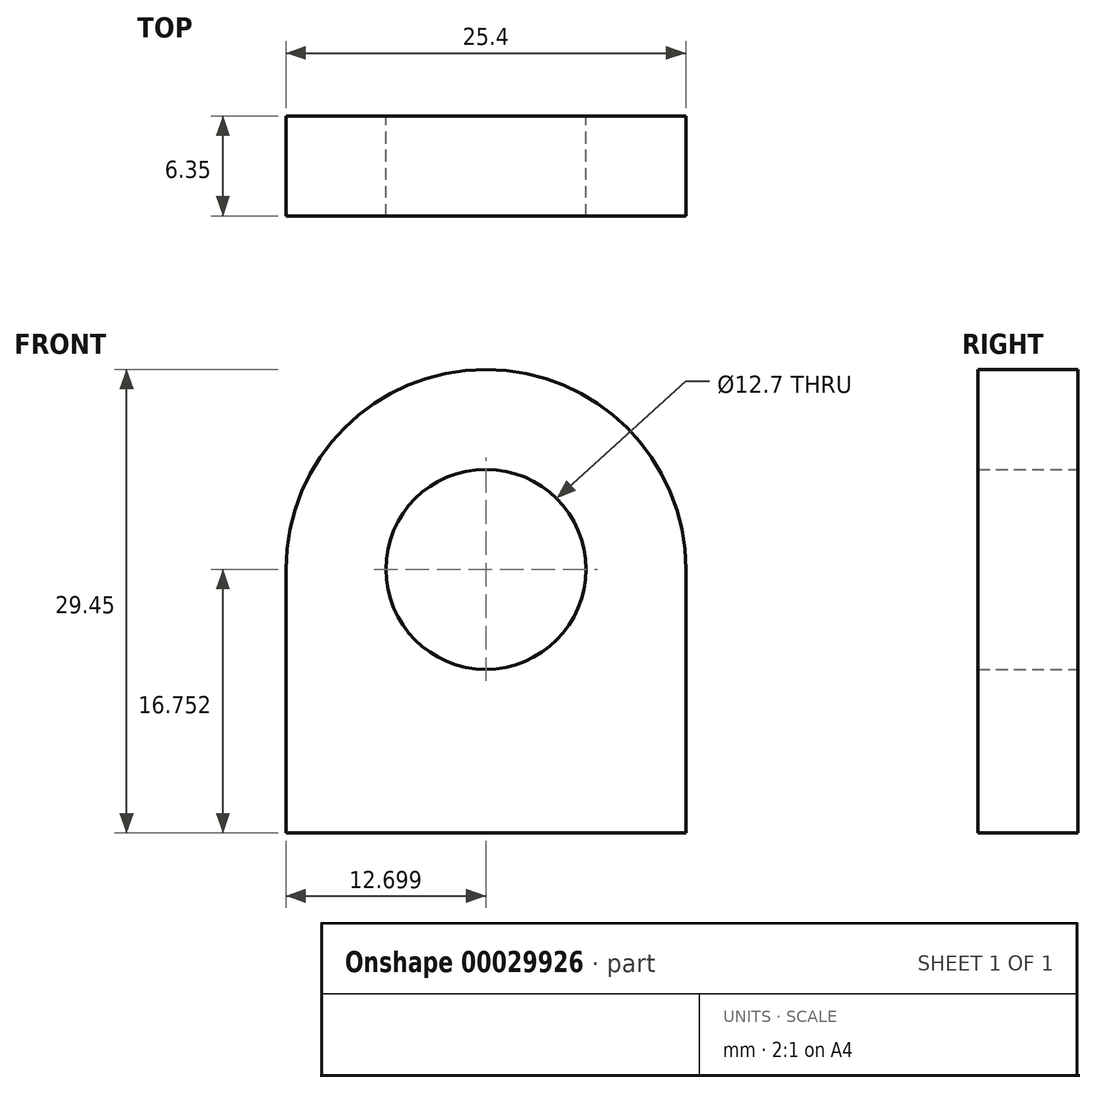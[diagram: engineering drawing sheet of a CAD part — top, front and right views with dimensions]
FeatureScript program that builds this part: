
annotation { "Feature Type Name" : "Feature", "Feature Type Description" : "" }
export const myFeature = defineFeature(function(context is Context, id is Id, definition is map)
    precondition{}
    {
        {
            var Q0;
            Q0=qCreatedBy(makeId("Front.planeOp"),FACE);
            var sketch = newSketch(context, id + "F0", { "sketchPlane" : qUnion([Q0])});
            skLineSegment(sketch, "E0.top", {"start": v(-5.45, 2.81) * mm, "end": v(19.95, 2.81) * mm});
            skLineSegment(sketch, "E0.left", {"start": v(-5.45, 19.56) * mm, "end": v(-5.45, 2.81) * mm});
            skLineSegment(sketch, "E0.right", {"start": v(19.95, 19.56) * mm, "end": v(19.95, 2.81) * mm});
            skArc(sketch, "E1", {"start": v(19.95, 19.56) * mm, "mid": v(7.25, 32.26) * mm, "end": v(-5.45, 19.56) * mm});
            skCircle(sketch, "E2", {"center": v(7.25, 19.56) * mm, "radius": 6.35 * mm});
            skSolve(sketch);
        }
        {
            var Q0;
            Q0 = qSketchRegion(id + "F0", true);
            extrude(context, id + "F1", {"entities" : qUnion([Q0]), "depth" : 6.35 * mm});
        }
    });
